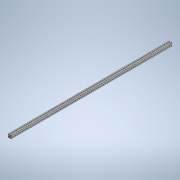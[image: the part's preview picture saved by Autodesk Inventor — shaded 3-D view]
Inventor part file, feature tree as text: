
AUTODESK INVENTOR PART (.ipt)
format: ipt  version: 2020 (Build 240168000, 168)  size: 463,360 bytes
history: native  units: mm
features: extrude x1, sketch x1
ambient origin geometry x8: Origin, YZ Plane, XZ Plane, XY Plane, X Axis, Y Axis, Z Axis, Center Point
bodies: Solid1 (feature_tree)
feature tree (2):
  extrude  "2020 Al T-S (1000mm)"  Depth=20.0mm
  sketch  "Sketch1"  dims[d0=20.0mm d1=20.0mm d2=4.0mm d5=6.0mm d7=1.0mm d8=2.0mm d9=2.0mm d10=3.1mm d11=3.1mm d12=1000.0mm d13=0.0mm d15=1.5mm d16=1.5mm d17=1.5mm d18=1.5mm d19=0.2mm d20=0.2mm d21=0.2mm d22=0.2mm d23=0.2mm d24=0.2mm d25=0.2mm d26=0.2mm d27=0.2mm d28=0.2mm d29=0.2mm d30=0.2mm d31=0.2mm d32=0.2mm d33=0.2mm d34=0.2mm d35=0.2mm d36=0.2mm d37=0.2mm d38=0.2mm d39=0.2mm d40=0.2mm d41=0.2mm]
